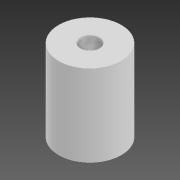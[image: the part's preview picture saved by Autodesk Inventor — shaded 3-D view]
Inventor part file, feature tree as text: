
AUTODESK INVENTOR PART (.ipt)
format: ipt  version: 2020 (Build 240168000, 168)  size: 79,872 bytes
history: native  units: in
note: dims shown in document units (in); Inventor stores cm internally (conversion verified against a paired STEP export)
features: extrude x1, sketch x1
ambient origin geometry x8: Origin, YZ Plane, XZ Plane, XY Plane, X Axis, Y Axis, Z Axis, Center Point
bodies: Solid1 (feature_tree)
feature tree (2):
  extrude  "Extrusion1"  Depth=0.5118in
  sketch  "Sketch1"  dims[d0=0.3937in d1=0.1181in d2=0.5118in d3=0.0in]
